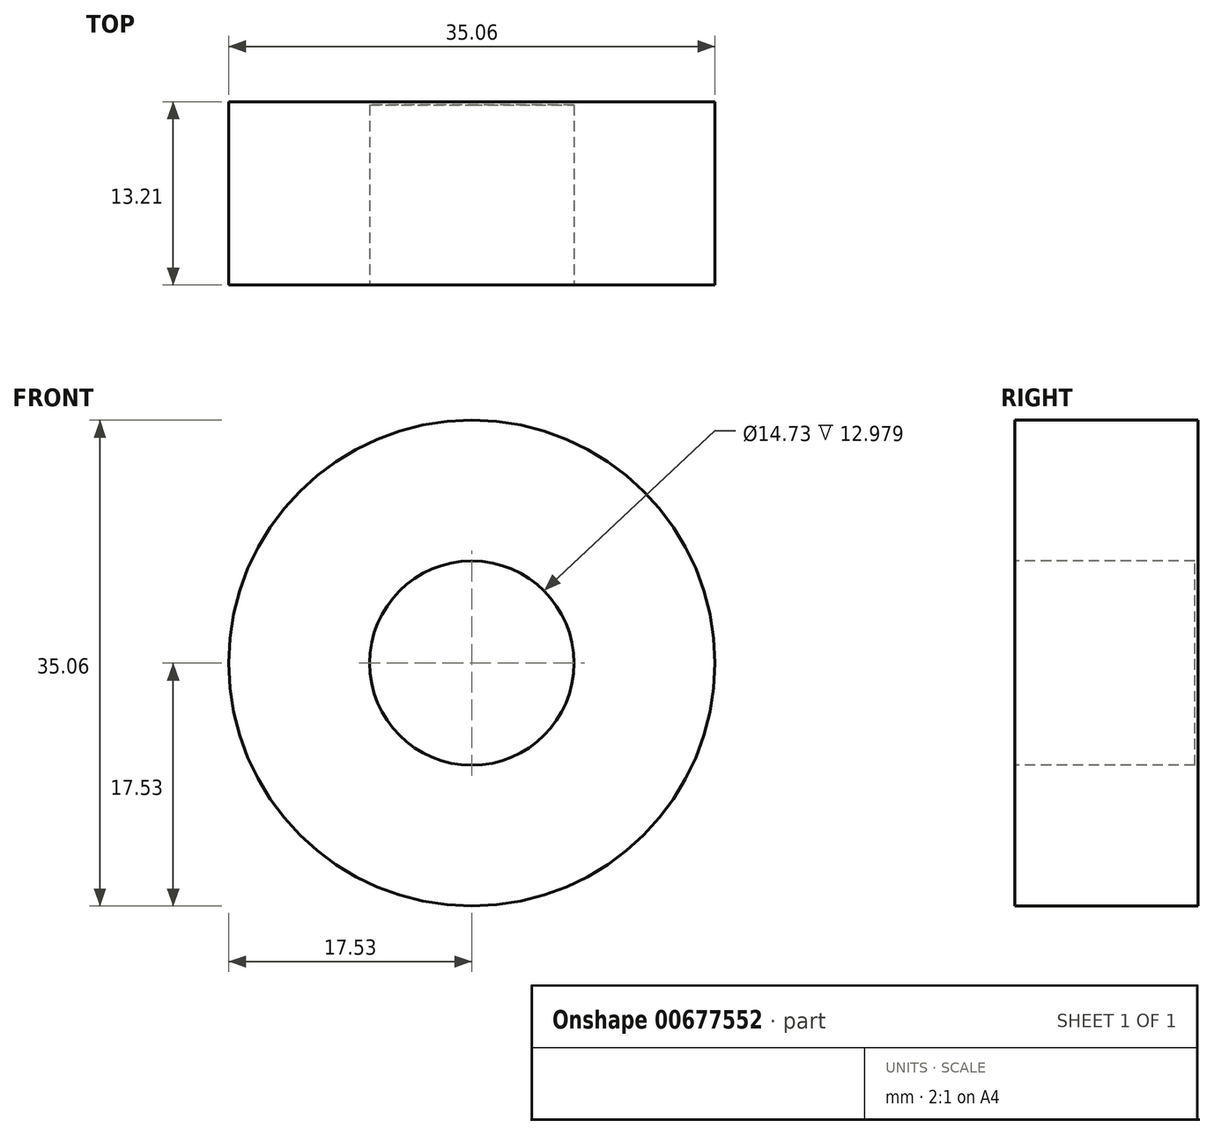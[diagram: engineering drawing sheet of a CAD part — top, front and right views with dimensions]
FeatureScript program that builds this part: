
annotation { "Feature Type Name" : "Feature", "Feature Type Description" : "" }
export const myFeature = defineFeature(function(context is Context, id is Id, definition is map)
    precondition{}
    {
        {
            var Q0;
            Q0=qCreatedBy(makeId("Front.planeOp"),FACE);
            var sketch = newSketch(context, id + "F0", { "sketchPlane" : qUnion([Q0])});
            skCircle(sketch, "E0", {"center": v(0, 0) * mm, "radius": 17.53 * mm});
            skSolve(sketch);
        }
        {
            var Q0;
            Q0=makeQuery(id+"F0.imprint","IMPRINT",FACE,{"disambiguationData":[TD([[makeQuery(id+"F0.imprint","IMPRINT",EDGE,{"derivedFrom":sQuery(id+"F0.wireOp",EDGE,"E0")}),1.0]])]});
            var Q1;
            Q1=makeQuery(id+"F0.imprint","IMPRINT",FACE,{"disambiguationData":[TD([[makeQuery(id+"F0.imprint","IMPRINT",EDGE,{"derivedFrom":sQuery(id+"F0.wireOp",EDGE,"5FJwf7ko-3Ny0-KsV4-GpGq-RGAoywbUZZXS")}),1.0]])]});
            extrude(context, id + "F1", {"entities" : qUnion([Q0, Q1]), "depth" : 13.2 * mm, "offsetDistance" : 25.4 * mm});
        }
        {
            var Q0;
            Q0=makeQuery(id+"F1.opExtrude","CAP_FACE",FACE,{"disambiguationData":[OSD([sQuery(id+"F0.wireOp",EDGE,"E0")])],"isStart":false});
            var sketch = newSketch(context, id + "F2", { "sketchPlane" : qUnion([Q0])});
            skCircle(sketch, "E1", {"center": v(0, 0) * mm, "radius": 7.37 * mm});
            skSolve(sketch);
        }
        {
            var Q0;
            Q0=makeQuery(id+"F2.imprint","IMPRINT",FACE,{"disambiguationData":[TD([[makeQuery(id+"F2.imprint","IMPRINT",EDGE,{"derivedFrom":sQuery(id+"F2.wireOp",EDGE,"E1")}),1.0]])]});
            extrude(context, id + "F3", {"entities" : qUnion([Q0]), "operationType" : NewBodyOperationType.REMOVE, "oppositeDirection" : true, "depth" : 12.98 * mm, "offsetDistance" : 25.4 * mm});
        }
    });
